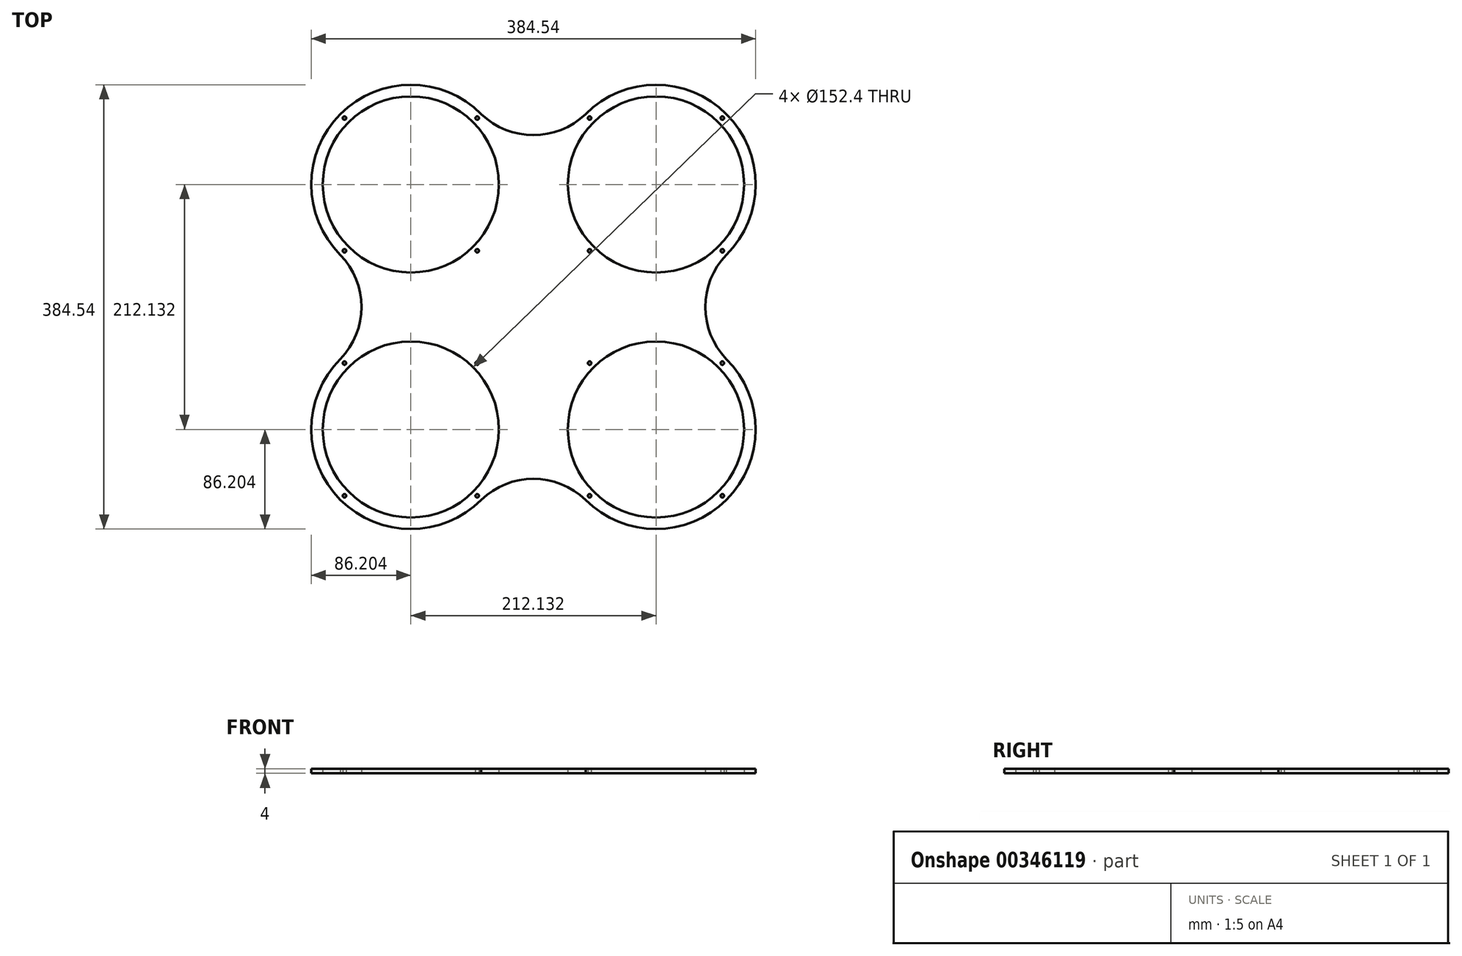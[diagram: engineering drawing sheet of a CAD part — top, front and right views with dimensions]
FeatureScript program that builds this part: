
annotation { "Feature Type Name" : "Feature", "Feature Type Description" : "" }
export const myFeature = defineFeature(function(context is Context, id is Id, definition is map)
    precondition{}
    {
        {
            var Q0;
            Q0=qCreatedBy(makeId("Top.planeOp"),FACE);
            var sketch = newSketch(context, id + "F0", { "sketchPlane" : qUnion([Q0])});
            skLineSegment(sketch, "E0", {"start": v(0, 0) * mm, "end": v(-106.07, 106.07) * mm, "construction": true});
            skCircle(sketch, "E1", {"center": v(-106.07, 106.07) * mm, "radius": 76.2 * mm});
            skPoint(sketch, "E2.middle", {"position": v(0, 0) * mm});
            skCircle(sketch, "E3.0", {"center": v(-106.07, 106.07) * mm, "radius": 86.2 * mm});
            skLineSegment(sketch, "E4", {"start": v(-45.11, 167.02) * mm, "end": v(-167.02, 45.11) * mm});
            skLineSegment(sketch, "E5.1.0", {"start": v(0, 0) * mm, "end": v(-106.07, -106.07) * mm, "construction": true});
            skCircle(sketch, "E5.1.1", {"center": v(-106.07, -106.07) * mm, "radius": 76.2 * mm});
            skCircle(sketch, "E5.1.2", {"center": v(-106.07, -106.07) * mm, "radius": 86.2 * mm});
            skLineSegment(sketch, "E5.1.3", {"start": v(-167.02, -45.11) * mm, "end": v(-45.11, -167.02) * mm});
            skPoint(sketch, "E5.1.5", {"position": v(-106.07, -106.07) * mm});
            skLineSegment(sketch, "E5.2.0", {"start": v(0, 0) * mm, "end": v(106.07, -106.07) * mm, "construction": true});
            skCircle(sketch, "E5.2.1", {"center": v(106.07, -106.07) * mm, "radius": 76.2 * mm});
            skCircle(sketch, "E5.2.2", {"center": v(106.07, -106.07) * mm, "radius": 86.2 * mm});
            skLineSegment(sketch, "E5.2.3", {"start": v(45.11, -167.02) * mm, "end": v(167.02, -45.11) * mm});
            skPoint(sketch, "E5.2.5", {"position": v(106.07, -106.07) * mm});
            skLineSegment(sketch, "E5.3.0", {"start": v(0, 0) * mm, "end": v(106.07, 106.07) * mm, "construction": true});
            skCircle(sketch, "E5.3.1", {"center": v(106.07, 106.07) * mm, "radius": 76.2 * mm});
            skCircle(sketch, "E5.3.2", {"center": v(106.07, 106.07) * mm, "radius": 86.2 * mm});
            skLineSegment(sketch, "E5.3.3", {"start": v(167.02, 45.11) * mm, "end": v(45.11, 167.02) * mm});
            skPoint(sketch, "E5.3.5", {"position": v(106.07, 106.07) * mm});
            skArc(sketch, "E6", {"start": v(-167.02, -45.11) * mm, "mid": v(-148.81, 0) * mm, "end": v(-167.02, 45.11) * mm});
            skArc(sketch, "E7.1.0", {"start": v(45.11, -167.02) * mm, "mid": v(0, -148.81) * mm, "end": v(-45.11, -167.02) * mm});
            skArc(sketch, "E7.2.0", {"start": v(167.02, 45.11) * mm, "mid": v(148.81, 0) * mm, "end": v(167.02, -45.11) * mm});
            skArc(sketch, "E7.3.0", {"start": v(-45.11, 167.02) * mm, "mid": v(0, 148.81) * mm, "end": v(45.11, 167.02) * mm});
            skLineSegment(sketch, "E8", {"start": v(-159.95, 52.18) * mm, "end": v(-167.02, 45.11) * mm, "construction": true});
            skPoint(sketch, "E9", {"position": v(-163.48, 48.65) * mm});
            skLineSegment(sketch, "E10", {"start": v(-45.11, 167.02) * mm, "end": v(-52.18, 159.95) * mm, "construction": true});
            skPoint(sketch, "E11", {"position": v(-48.65, 163.48) * mm});
            skLineSegment(sketch, "E12", {"start": v(-106.07, 106.07) * mm, "end": v(-159.95, 159.95) * mm, "construction": true});
            skLineSegment(sketch, "E13", {"start": v(-159.95, 159.95) * mm, "end": v(-167.02, 167.02) * mm, "construction": true});
            skPoint(sketch, "E14", {"position": v(-163.48, 163.48) * mm});
            skLineSegment(sketch, "E15", {"start": v(-52.18, 52.18) * mm, "end": v(-45.11, 45.11) * mm, "construction": true});
            skPoint(sketch, "E16", {"position": v(-48.65, 48.65) * mm});
            skPoint(sketch, "E17.1.0", {"position": v(-163.48, -163.48) * mm});
            skPoint(sketch, "E17.1.1", {"position": v(-163.48, -48.65) * mm});
            skPoint(sketch, "E17.1.2", {"position": v(-48.65, -163.48) * mm});
            skPoint(sketch, "E17.1.3", {"position": v(-48.65, -48.65) * mm});
            skPoint(sketch, "E17.2.0", {"position": v(163.48, -163.48) * mm});
            skPoint(sketch, "E17.2.1", {"position": v(48.65, -163.48) * mm});
            skPoint(sketch, "E17.2.2", {"position": v(163.48, -48.65) * mm});
            skPoint(sketch, "E17.2.3", {"position": v(48.65, -48.65) * mm});
            skPoint(sketch, "E17.3.0", {"position": v(163.48, 163.48) * mm});
            skPoint(sketch, "E17.3.1", {"position": v(163.48, 48.65) * mm});
            skPoint(sketch, "E17.3.2", {"position": v(48.65, 163.48) * mm});
            skPoint(sketch, "E17.3.3", {"position": v(48.65, 48.65) * mm});
            skSolve(sketch);
        }
        {
            var Q0;
            {var subQ0=sQuery(id+"F0.wireOp",EDGE,"E4");var subQ1=sQuery(id+"F0.wireOp",EDGE,"E1");var subQ2=makeQuery(id+"F0.imprint","INTERSECT",VERTEX,{"disambiguationData":[OD(0.0)],"derivedFrom":[subQ1,subQ0]});Q0=makeQuery(id+"F0.imprint","IMPRINT",FACE,{"disambiguationData":[TD([[makeQuery(id+"F0.imprint","IMPRINT",EDGE,{"disambiguationData":[TD([[subQ2,-1.0]])],"derivedFrom":subQ1}),-1.0]])]});}
            var Q1;
            {var subQ0=sQuery(id+"F0.wireOp",EDGE,"E4");var subQ1=sQuery(id+"F0.wireOp",EDGE,"E1");var subQ2=makeQuery(id+"F0.imprint","INTERSECT",VERTEX,{"disambiguationData":[OD(0.0)],"derivedFrom":[subQ1,subQ0]});Q1=makeQuery(id+"F0.imprint","IMPRINT",FACE,{"disambiguationData":[TD([[makeQuery(id+"F0.imprint","IMPRINT",EDGE,{"disambiguationData":[TD([[subQ2,1.0]])],"derivedFrom":subQ1}),-1.0]])]});}
            var Q2;
            {var subQ7=sQuery(id+"F0.wireOp",EDGE,"E6");Q2=makeQuery(id+"F0.imprint","IMPRINT",FACE,{"disambiguationData":[TD([[makeQuery(id+"F0.imprint","IMPRINT",EDGE,{"derivedFrom":subQ7}),-1.0]])]});}
            var Q3;
            {var subQ0=sQuery(id+"F0.wireOp",EDGE,"E5.3.3");var subQ1=sQuery(id+"F0.wireOp",EDGE,"E5.3.1");var subQ2=makeQuery(id+"F0.imprint","INTERSECT",VERTEX,{"disambiguationData":[OD(0.0)],"derivedFrom":[subQ1,subQ0]});Q3=makeQuery(id+"F0.imprint","IMPRINT",FACE,{"disambiguationData":[TD([[makeQuery(id+"F0.imprint","IMPRINT",EDGE,{"disambiguationData":[TD([[subQ2,1.0]])],"derivedFrom":subQ1}),-1.0]])]});}
            var Q4;
            {var subQ0=sQuery(id+"F0.wireOp",EDGE,"E5.3.3");var subQ1=sQuery(id+"F0.wireOp",EDGE,"E5.3.1");var subQ2=makeQuery(id+"F0.imprint","INTERSECT",VERTEX,{"disambiguationData":[OD(0.0)],"derivedFrom":[subQ1,subQ0]});Q4=makeQuery(id+"F0.imprint","IMPRINT",FACE,{"disambiguationData":[TD([[makeQuery(id+"F0.imprint","IMPRINT",EDGE,{"disambiguationData":[TD([[subQ2,-1.0]])],"derivedFrom":subQ1}),-1.0]])]});}
            var Q5;
            {var subQ0=sQuery(id+"F0.wireOp",EDGE,"E5.2.3");var subQ1=sQuery(id+"F0.wireOp",EDGE,"E5.2.1");var subQ2=makeQuery(id+"F0.imprint","INTERSECT",VERTEX,{"disambiguationData":[OD(0.0)],"derivedFrom":[subQ1,subQ0]});Q5=makeQuery(id+"F0.imprint","IMPRINT",FACE,{"disambiguationData":[TD([[makeQuery(id+"F0.imprint","IMPRINT",EDGE,{"disambiguationData":[TD([[subQ2,1.0]])],"derivedFrom":subQ1}),-1.0]])]});}
            var Q6;
            {var subQ0=sQuery(id+"F0.wireOp",EDGE,"E5.2.3");var subQ1=sQuery(id+"F0.wireOp",EDGE,"E5.2.1");var subQ2=makeQuery(id+"F0.imprint","INTERSECT",VERTEX,{"disambiguationData":[OD(0.0)],"derivedFrom":[subQ1,subQ0]});Q6=makeQuery(id+"F0.imprint","IMPRINT",FACE,{"disambiguationData":[TD([[makeQuery(id+"F0.imprint","IMPRINT",EDGE,{"disambiguationData":[TD([[subQ2,-1.0]])],"derivedFrom":subQ1}),-1.0]])]});}
            var Q7;
            {var subQ0=sQuery(id+"F0.wireOp",EDGE,"E5.1.3");var subQ1=sQuery(id+"F0.wireOp",EDGE,"E5.1.1");var subQ2=makeQuery(id+"F0.imprint","INTERSECT",VERTEX,{"disambiguationData":[OD(0.0)],"derivedFrom":[subQ1,subQ0]});Q7=makeQuery(id+"F0.imprint","IMPRINT",FACE,{"disambiguationData":[TD([[makeQuery(id+"F0.imprint","IMPRINT",EDGE,{"disambiguationData":[TD([[subQ2,1.0]])],"derivedFrom":subQ1}),-1.0]])]});}
            var Q8;
            {var subQ0=sQuery(id+"F0.wireOp",EDGE,"E5.1.3");var subQ1=sQuery(id+"F0.wireOp",EDGE,"E5.1.1");var subQ2=makeQuery(id+"F0.imprint","INTERSECT",VERTEX,{"disambiguationData":[OD(0.0)],"derivedFrom":[subQ1,subQ0]});Q8=makeQuery(id+"F0.imprint","IMPRINT",FACE,{"disambiguationData":[TD([[makeQuery(id+"F0.imprint","IMPRINT",EDGE,{"disambiguationData":[TD([[subQ2,-1.0]])],"derivedFrom":subQ1}),-1.0]])]});}
            extrude(context, id + "F1", {"entities" : qUnion([Q0, Q1, Q2, Q3, Q4, Q5, Q6, Q7, Q8]), "depth" : 4 * mm});
        }
        {
            var Q0;
            Q0=sQuery(id+"F0.wireOp",VERTEX,"E14");
            var Q1;
            Q1=sQuery(id+"F0.wireOp",VERTEX,"E11");
            var Q2;
            Q2=sQuery(id+"F0.wireOp",VERTEX,"E16");
            var Q3;
            Q3=sQuery(id+"F0.wireOp",VERTEX,"E9");
            var Q4;
            Q4=sQuery(id+"F0.wireOp",VERTEX,"E17.1.1");
            var Q5;
            Q5=sQuery(id+"F0.wireOp",VERTEX,"E17.1.3");
            var Q6;
            Q6=sQuery(id+"F0.wireOp",VERTEX,"E17.1.2");
            var Q7;
            Q7=sQuery(id+"F0.wireOp",VERTEX,"E17.1.0");
            var Q8;
            Q8=sQuery(id+"F0.wireOp",VERTEX,"E17.2.1");
            var Q9;
            Q9=sQuery(id+"F0.wireOp",VERTEX,"E17.2.3");
            var Q10;
            Q10=sQuery(id+"F0.wireOp",VERTEX,"E17.2.2");
            var Q11;
            Q11=sQuery(id+"F0.wireOp",VERTEX,"E17.2.0");
            var Q12;
            Q12=sQuery(id+"F0.wireOp",VERTEX,"E17.3.0");
            var Q13;
            Q13=sQuery(id+"F0.wireOp",VERTEX,"E17.3.1");
            var Q14;
            Q14=sQuery(id+"F0.wireOp",VERTEX,"E17.3.3");
            var Q15;
            Q15=sQuery(id+"F0.wireOp",VERTEX,"E17.3.2");
            var Q16;
            Q16=makeQuery(id+"F1.opExtrude","SWEPT_BODY",BODY,{"disambiguationData":[OSD([sQuery(id+"F0.wireOp",EDGE,"E1"),sQuery(id+"F0.wireOp",EDGE,"E3.0"),sQuery(id+"F0.wireOp",EDGE,"E5.1.1"),sQuery(id+"F0.wireOp",EDGE,"E5.1.2"),sQuery(id+"F0.wireOp",EDGE,"E5.2.1"),sQuery(id+"F0.wireOp",EDGE,"E5.2.2"),sQuery(id+"F0.wireOp",EDGE,"E5.3.1"),sQuery(id+"F0.wireOp",EDGE,"E5.3.2"),sQuery(id+"F0.wireOp",EDGE,"E6"),sQuery(id+"F0.wireOp",EDGE,"E7.1.0"),sQuery(id+"F0.wireOp",EDGE,"E7.2.0"),sQuery(id+"F0.wireOp",EDGE,"E7.3.0")])]});
            hole(context, id + "F2", {"style" : HoleStyle.SIMPLE, "endStyle" : HoleEndStyle.THROUGH, "oppositeDirection" : true, "holeDiameter" : 3 * mm, "isTappedThrough" : true, "tappedDepth" : 12 * mm, "tapClearance" : 3, "locations" : qUnion([Q0, Q1, Q2, Q3, Q4, Q5, Q6, Q7, Q8, Q9, Q10, Q11, Q12, Q13, Q14, Q15]), "scope" : qUnion([Q16])});
        }
    });
